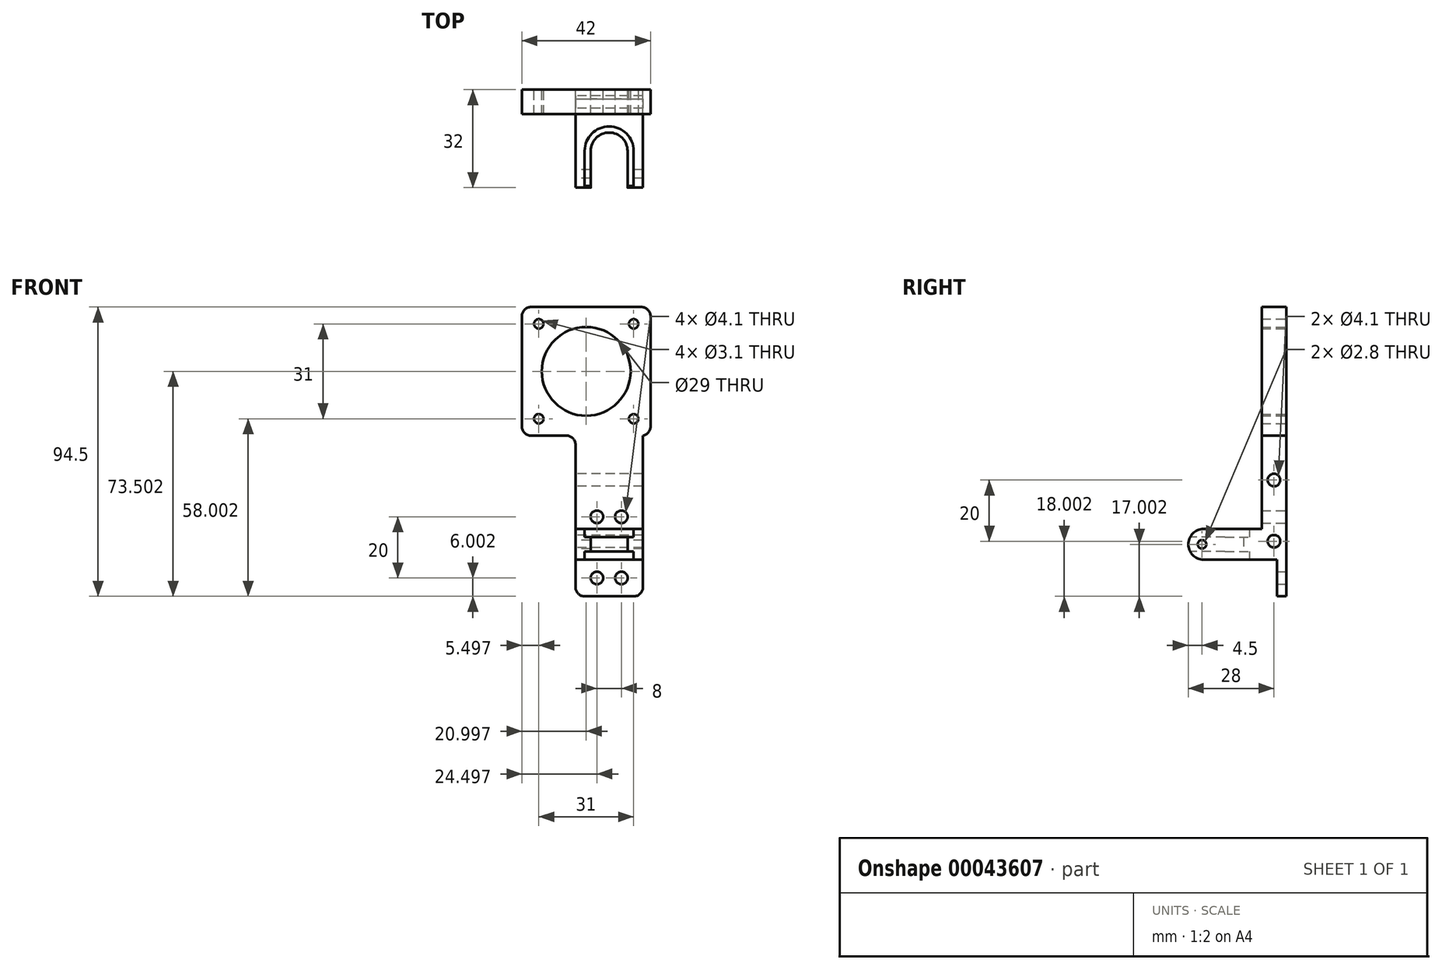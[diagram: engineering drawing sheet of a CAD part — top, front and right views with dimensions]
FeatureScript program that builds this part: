
annotation { "Feature Type Name" : "Feature", "Feature Type Description" : "" }
export const myFeature = defineFeature(function(context is Context, id is Id, definition is map)
    precondition{}
    {
        {
            var Q0;
            Q0=qCreatedBy(makeId("Front.planeOp"),FACE);
            var sketch = newSketch(context, id + "F0", { "sketchPlane" : qUnion([Q0])});
            skLineSegment(sketch, "E0.bottom", {"start": v(-39.92, 48.94) * mm, "end": v(-17.92, 48.94) * mm});
            skLineSegment(sketch, "E0.top", {"start": v(-39.92, 6.94) * mm, "end": v(-17.92, 6.94) * mm});
            skLineSegment(sketch, "E0.left", {"start": v(-39.92, 48.94) * mm, "end": v(-39.92, 6.94) * mm});
            skLineSegment(sketch, "E0.right", {"start": v(-17.92, 48.94) * mm, "end": v(-17.92, 6.94) * mm});
            skPoint(sketch, "E1", {"position": v(-32.92, 12.94) * mm});
            skPoint(sketch, "E2", {"position": v(-24.92, 12.94) * mm});
            skPoint(sketch, "E3", {"position": v(-24.92, 32.94) * mm});
            skPoint(sketch, "E4", {"position": v(-32.92, 32.94) * mm});
            skLineSegment(sketch, "E5", {"start": v(-39.92, 23.94) * mm, "end": v(-17.92, 23.94) * mm, "construction": true});
            skSolve(sketch);
        }
        {
            var Q0;
            Q0=makeQuery(id+"F0.imprint","IMPRINT",FACE,{"disambiguationData":[TD([[makeQuery(id+"F0.imprint","IMPRINT",EDGE,{"derivedFrom":sQuery(id+"F0.wireOp",EDGE,"E0.bottom")}),-1.0]])]});
            extrude(context, id + "F1", {"entities" : qUnion([Q0]), "depth" : 3 * mm});
        }
        {
            var Q0;
            Q0=makeQuery(id+"F1.opExtrude","SWEPT_FACE",FACE,{"disambiguationData":[OSD([sQuery(id+"F0.wireOp",EDGE,"E0.left")])]});
            var sketch = newSketch(context, id + "F2", { "sketchPlane" : qUnion([Q0])});
            skLineSegment(sketch, "E6.bottom", {"start": v(0, 18.94) * mm, "end": v(8, 18.94) * mm});
            skLineSegment(sketch, "E6.top", {"start": v(0, 48.94) * mm, "end": v(8, 48.94) * mm});
            skLineSegment(sketch, "E6.left", {"start": v(0, 18.94) * mm, "end": v(0, 48.94) * mm});
            skLineSegment(sketch, "E6.right", {"start": v(8, 18.94) * mm, "end": v(8, 48.94) * mm});
            skPoint(sketch, "E7", {"position": v(4, 44.94) * mm});
            skPoint(sketch, "E8", {"position": v(4, 24.94) * mm});
            skSolve(sketch);
        }
        {
            var Q0;
            {var subQ0=sQuery(id+"F2.wireOp",EDGE,"E6.left");Q0=makeQuery(id+"F2.imprint","IMPRINT",FACE,{"disambiguationData":[TD([[makeQuery(id+"F2.imprint","IMPRINT",EDGE,{"derivedFrom":subQ0}),1.0]])]});}
            var Q1;
            {var subQ0=sQuery(id+"F2.wireOp",EDGE,"E6.right");Q1=makeQuery(id+"F2.imprint","IMPRINT",FACE,{"disambiguationData":[TD([[makeQuery(id+"F2.imprint","IMPRINT",EDGE,{"derivedFrom":subQ0}),1.0]])]});}
            extrude(context, id + "F3", {"entities" : qUnion([Q0, Q1]), "operationType" : NewBodyOperationType.ADD, "oppositeDirection" : true, "depth" : 22 * mm});
        }
        {
            var Q0;
            Q0=sQuery(id+"F0.wireOp",VERTEX,"E2");
            var Q1;
            Q1=sQuery(id+"F0.wireOp",VERTEX,"E1");
            var Q2;
            Q2=sQuery(id+"F0.wireOp",VERTEX,"E4");
            var Q3;
            Q3=sQuery(id+"F0.wireOp",VERTEX,"E3");
            var Q4;
            Q4=makeQuery(id+"F1.opExtrude","SWEPT_BODY",BODY,{"disambiguationData":[OSD([sQuery(id+"F0.wireOp",EDGE,"E0.bottom"),sQuery(id+"F0.wireOp",EDGE,"E0.top"),sQuery(id+"F0.wireOp",EDGE,"E0.left"),sQuery(id+"F0.wireOp",EDGE,"E0.right")])]});
            hole(context, id + "F4", {"style" : HoleStyle.SIMPLE, "holeDiameter" : 4.1 * mm, "endStyle" : HoleEndStyle.THROUGH, "oppositeDirection" : true, "locations" : qUnion([Q0, Q1, Q2, Q3]), "scope" : qUnion([Q4])});
        }
        {
            var Q0;
            Q0=sQuery(id+"F0.wireOp",EDGE,"E5");
            cPlane(context, id + "F5", {"entities" : qUnion([Q0]), "cplaneType" : CPlaneType.LINE_ANGLE, "offset" : 150 * mm, "angle" : 90 * degree, "width" : 150 * mm, "height" : 150 * mm});
        }
        {
            var Q0;
            Q0=qCreatedBy(id+"F5.planeOp",FACE);
            var sketch = newSketch(context, id + "F6", { "sketchPlane" : qUnion([Q0])});
            skPoint(sketch, "E9", {"position": v(-28.92, -20) * mm});
            skCircle(sketch, "E10", {"center": v(-28.92, -20) * mm, "radius": 6 * mm});
            skCircle(sketch, "E11", {"center": v(-28.92, -20) * mm, "radius": 8 * mm});
            skLineSegment(sketch, "E12.top", {"start": v(-39.92, 0) * mm, "end": v(-17.92, 0) * mm});
            skLineSegment(sketch, "E13.bottom", {"start": v(-39.92, -32) * mm, "end": v(-17.92, -32) * mm});
            skLineSegment(sketch, "E13.left", {"start": v(-39.92, -32) * mm, "end": v(-39.92, 0) * mm});
            skLineSegment(sketch, "E13.right", {"start": v(-17.92, -32) * mm, "end": v(-17.92, 0) * mm});
            skLineSegment(sketch, "E14", {"start": v(-34.92, -20) * mm, "end": v(-34.92, -32) * mm});
            skLineSegment(sketch, "E15", {"start": v(-36.92, -20) * mm, "end": v(-36.92, -32) * mm});
            skLineSegment(sketch, "E16", {"start": v(-22.92, -20) * mm, "end": v(-22.92, -32) * mm});
            skLineSegment(sketch, "E17", {"start": v(-20.92, -20) * mm, "end": v(-20.92, -32) * mm});
            skPoint(sketch, "E18", {"position": v(-28.92, -27.5) * mm});
            skPoint(sketch, "E18.positionSnap0", {"position": v(-28.92, -32) * mm});
            skSolve(sketch);
        }
        {
            var Q0;
            Q0=makeQuery(id+"F6.imprint","IMPRINT",FACE,{"disambiguationData":[TD([[makeQuery(id+"F6.imprint","IMPRINT",EDGE,{"derivedFrom":sQuery(id+"F6.wireOp",EDGE,"E12.top")}),-1.0]])]});
            var Q1;
            Q1=sQuery(id+"F6.wireOp",EDGE,"E12.bottom");
            extrude(context, id + "F7", {"entities" : qUnion([Q0]), "operationType" : NewBodyOperationType.ADD, "surfaceEntities" : qUnion([Q1]), "endBound" : BoundingType.SYMMETRIC, "depth" : 10 * mm});
        }
        {
            var Q0;
            {var subQ5=sQuery(id+"F6.wireOp",EDGE,"E14");var subQ7=sQuery(id+"F6.wireOp",EDGE,"E10");var subQ9=makeQuery(id+"F6.imprint","INTERSECT",VERTEX,{"derivedFrom":[subQ7,subQ5]});Q0=makeQuery(id+"F6.imprint","IMPRINT",FACE,{"disambiguationData":[TD([[makeQuery(id+"F6.imprint","IMPRINT",EDGE,{"disambiguationData":[TD([[subQ9,1.0]])],"derivedFrom":subQ7}),-1.0]])]});}
            var Q1;
            {var subQ0=sQuery(id+"F6.wireOp",EDGE,"E15");Q1=makeQuery(id+"F6.imprint","IMPRINT",FACE,{"disambiguationData":[TD([[makeQuery(id+"F6.imprint","IMPRINT",EDGE,{"derivedFrom":subQ0}),1.0]])]});}
            var Q2;
            {var subQ0=sQuery(id+"F6.wireOp",EDGE,"E17");Q2=makeQuery(id+"F6.imprint","IMPRINT",FACE,{"disambiguationData":[TD([[makeQuery(id+"F6.imprint","IMPRINT",EDGE,{"derivedFrom":subQ0}),-1.0]])]});}
            extrude(context, id + "F8", {"entities" : qUnion([Q0, Q1, Q2]), "operationType" : NewBodyOperationType.ADD, "endBound" : BoundingType.SYMMETRIC, "depth" : 4.65 * mm});
        }
        {
            var Q0;
            {var subQ0=sQuery(id+"F6.wireOp",EDGE,"E13.bottom");Q0=makeQuery(id+"F7.opExtrude","CAP_EDGE",EDGE,{"disambiguationData":[OSD([subQ0]),TDD([makeQuery(id+"F6.imprint","IMPRINT",EDGE,{"disambiguationData":[TD([[makeQuery(id+"F6.imprint","INTERSECT",VERTEX,{"derivedFrom":[subQ0,sQuery(id+"F6.wireOp",EDGE,"E13.left")]}),-1.0]])],"derivedFrom":subQ0})])],"isStart":false});}
            var Q1;
            {var subQ0=sQuery(id+"F6.wireOp",EDGE,"E13.bottom");Q1=makeQuery(id+"F7.opExtrude","CAP_EDGE",EDGE,{"disambiguationData":[OSD([subQ0]),TDD([makeQuery(id+"F6.imprint","IMPRINT",EDGE,{"disambiguationData":[TD([[makeQuery(id+"F6.imprint","INTERSECT",VERTEX,{"derivedFrom":[subQ0,sQuery(id+"F6.wireOp",EDGE,"E13.left")]}),-1.0]])],"derivedFrom":subQ0})])],"isStart":true});}
            var Q2;
            {var subQ0=sQuery(id+"F6.wireOp",EDGE,"E13.bottom");Q2=makeQuery(id+"F7.opExtrude","CAP_EDGE",EDGE,{"disambiguationData":[OSD([subQ0]),TDD([makeQuery(id+"F6.imprint","IMPRINT",EDGE,{"disambiguationData":[TD([[makeQuery(id+"F6.imprint","INTERSECT",VERTEX,{"derivedFrom":[subQ0,sQuery(id+"F6.wireOp",EDGE,"E13.right")]}),1.0]])],"derivedFrom":subQ0})])],"isStart":true});}
            var Q3;
            {var subQ0=sQuery(id+"F6.wireOp",EDGE,"E13.bottom");Q3=makeQuery(id+"F7.opExtrude","CAP_EDGE",EDGE,{"disambiguationData":[OSD([subQ0]),TDD([makeQuery(id+"F6.imprint","IMPRINT",EDGE,{"disambiguationData":[TD([[makeQuery(id+"F6.imprint","INTERSECT",VERTEX,{"derivedFrom":[subQ0,sQuery(id+"F6.wireOp",EDGE,"E13.right")]}),1.0]])],"derivedFrom":subQ0})])],"isStart":false});}
            fillet(context, id + "F9", {"entities" : qUnion([Q0, Q1, Q2, Q3]), "radius" : 5 * mm, "tangentPropagation" : true, "allowEdgeOverflow" : false});
        }
        {
            var Q0;
            Q0=makeQuery(id+"F7.boolean.opBoolean","MERGE",FACE,{"derivedFrom":[makeQuery(id+"F3.boolean.opBoolean","MERGE",FACE,{"derivedFrom":[makeQuery(id+"F1.opExtrude","SWEPT_FACE",FACE,{"disambiguationData":[OSD([sQuery(id+"F0.wireOp",EDGE,"E0.left")])]}),makeQuery(id+"F3.opExtrude","CAP_FACE",FACE,{"disambiguationData":[OSD([sQuery(id+"F2.wireOp",EDGE,"E6.bottom"),sQuery(id+"F2.wireOp",EDGE,"E6.top"),sQuery(id+"F2.wireOp",EDGE,"E6.left"),sQuery(id+"F2.wireOp",EDGE,"E6.right")])],"isStart":true})]}),makeQuery(id+"F7.opExtrude","SWEPT_FACE",FACE,{"disambiguationData":[OSD([sQuery(id+"F6.wireOp",EDGE,"E13.left")])]})]});
            var sketch = newSketch(context, id + "F10", { "sketchPlane" : qUnion([Q0])});
            skPoint(sketch, "E19", {"position": v(27.5, 23.94) * mm});
            skSolve(sketch);
        }
        {
            var Q0;
            Q0=sQuery(id+"F2.wireOp",VERTEX,"E7");
            var Q1;
            Q1=sQuery(id+"F2.wireOp",VERTEX,"E8");
            var Q2;
            Q2=makeQuery(id+"F1.opExtrude","SWEPT_BODY",BODY,{"disambiguationData":[OSD([sQuery(id+"F0.wireOp",EDGE,"E0.bottom"),sQuery(id+"F0.wireOp",EDGE,"E0.top"),sQuery(id+"F0.wireOp",EDGE,"E0.left"),sQuery(id+"F0.wireOp",EDGE,"E0.right")])]});
            hole(context, id + "F11", {"style" : HoleStyle.SIMPLE, "holeDiameter" : 4.1 * mm, "endStyle" : HoleEndStyle.THROUGH, "locations" : qUnion([Q0, Q1]), "scope" : qUnion([Q2])});
        }
        {
            var Q0;
            Q0=sQuery(id+"F10.wireOp",VERTEX,"E19");
            var Q1;
            Q1=makeQuery(id+"F1.opExtrude","SWEPT_BODY",BODY,{"disambiguationData":[OSD([sQuery(id+"F0.wireOp",EDGE,"E0.bottom"),sQuery(id+"F0.wireOp",EDGE,"E0.top"),sQuery(id+"F0.wireOp",EDGE,"E0.left"),sQuery(id+"F0.wireOp",EDGE,"E0.right")])]});
            hole(context, id + "F12", {"style" : HoleStyle.SIMPLE, "holeDiameter" : 2.8 * mm, "endStyle" : HoleEndStyle.THROUGH, "locations" : qUnion([Q0]), "scope" : qUnion([Q1])});
        }
        {
            var Q0;
            Q0=qCreatedBy(makeId("Front.planeOp"),FACE);
            var sketch = newSketch(context, id + "F13", { "sketchPlane" : qUnion([Q0])});
            skLineSegment(sketch, "E20.bottom", {"start": v(-39.92, 48.94) * mm, "end": v(-17.92, 48.94) * mm});
            skLineSegment(sketch, "E20.top", {"start": v(-39.92, 59.44) * mm, "end": v(-17.92, 59.44) * mm});
            skLineSegment(sketch, "E20.left", {"start": v(-39.92, 48.94) * mm, "end": v(-39.92, 59.44) * mm});
            skLineSegment(sketch, "E20.right", {"start": v(-17.92, 48.94) * mm, "end": v(-17.92, 59.44) * mm});
            skPoint(sketch, "E21.firstSnap0", {"position": v(-28.92, 59.44) * mm});
            skLineSegment(sketch, "E21.bottom", {"start": v(-15.42, 59.44) * mm, "end": v(-57.42, 59.44) * mm});
            skLineSegment(sketch, "E21.top", {"start": v(-15.42, 101.44) * mm, "end": v(-57.42, 101.44) * mm});
            skLineSegment(sketch, "E21.left", {"start": v(-15.42, 59.44) * mm, "end": v(-15.42, 101.44) * mm});
            skLineSegment(sketch, "E21.right", {"start": v(-57.42, 59.44) * mm, "end": v(-57.42, 101.44) * mm});
            skPoint(sketch, "E22", {"position": v(-36.42, 80.44) * mm});
            skPoint(sketch, "E23", {"position": v(-51.92, 95.94) * mm});
            skPoint(sketch, "E24", {"position": v(-51.92, 64.94) * mm});
            skPoint(sketch, "E25", {"position": v(-20.92, 64.94) * mm});
            skPoint(sketch, "E26", {"position": v(-20.92, 95.94) * mm});
            skLineSegment(sketch, "E27", {"start": v(-28.92, 101.44) * mm, "end": v(-28.92, 59.44) * mm, "construction": true});
            skLineSegment(sketch, "E28", {"start": v(-28.92, 7.33) * mm, "end": v(-28.92, 59.44) * mm, "construction": true});
            skSolve(sketch);
        }
        {
            var Q0;
            Q0=makeQuery(id+"F13.imprint","IMPRINT",FACE,{"disambiguationData":[TD([[makeQuery(id+"F13.imprint","IMPRINT",EDGE,{"derivedFrom":sQuery(id+"F13.wireOp",EDGE,"E21.top")}),1.0]])]});
            var Q1;
            Q1=makeQuery(id+"F13.imprint","IMPRINT",FACE,{"disambiguationData":[TD([[makeQuery(id+"F13.imprint","IMPRINT",EDGE,{"derivedFrom":sQuery(id+"F13.wireOp",EDGE,"E20.bottom")}),1.0]])]});
            extrude(context, id + "F14", {"entities" : qUnion([Q0, Q1]), "operationType" : NewBodyOperationType.ADD, "depth" : 8 * mm});
        }
        {
            var Q0;
            Q0=makeQuery(id+"F14.opExtrude","SWEPT_EDGE",EDGE,{"disambiguationData":[OSD([sQuery(id+"F13.wireOp",EDGE,"E21.top"),sQuery(id+"F13.wireOp",EDGE,"E21.right")])]});
            var Q1;
            Q1=makeQuery(id+"F14.opExtrude","SWEPT_EDGE",EDGE,{"disambiguationData":[OSD([sQuery(id+"F13.wireOp",EDGE,"E21.bottom"),sQuery(id+"F13.wireOp",EDGE,"E21.right")])]});
            var Q2;
            Q2=makeQuery(id+"F14.opExtrude","SWEPT_EDGE",EDGE,{"disambiguationData":[OSD([sQuery(id+"F13.wireOp",EDGE,"E21.top"),sQuery(id+"F13.wireOp",EDGE,"E21.left")])]});
            var Q3;
            Q3=makeQuery(id+"F1.opExtrude","SWEPT_EDGE",EDGE,{"disambiguationData":[OSD([sQuery(id+"F0.wireOp",EDGE,"E0.top"),sQuery(id+"F0.wireOp",EDGE,"E0.left")])]});
            var Q4;
            Q4=makeQuery(id+"F1.opExtrude","SWEPT_EDGE",EDGE,{"disambiguationData":[OSD([sQuery(id+"F0.wireOp",EDGE,"E0.top"),sQuery(id+"F0.wireOp",EDGE,"E0.right")])]});
            var Q5;
            Q5=makeQuery(id+"F14.opExtrude","SWEPT_EDGE",EDGE,{"disambiguationData":[OSD([sQuery(id+"F13.wireOp",EDGE,"E20.left"),sQuery(id+"F13.wireOp",EDGE,"E21.bottom")])]});
            var Q6;
            Q6=makeQuery(id+"F14.opExtrude","SWEPT_EDGE",EDGE,{"disambiguationData":[OSD([sQuery(id+"F13.wireOp",EDGE,"E21.bottom"),sQuery(id+"F13.wireOp",EDGE,"E21.left")])]});
            fillet(context, id + "F15", {"entities" : qUnion([Q0, Q1, Q2, Q3, Q4, Q5, Q6]), "radius" : 3 * mm, "tangentPropagation" : true, "allowEdgeOverflow" : false});
        }
        {
            var Q0;
            Q0=sQuery(id+"F13.wireOp",VERTEX,"E22");
            var Q1;
            Q1=makeQuery(id+"F1.opExtrude","SWEPT_BODY",BODY,{"disambiguationData":[OSD([sQuery(id+"F0.wireOp",EDGE,"E0.bottom"),sQuery(id+"F0.wireOp",EDGE,"E0.top"),sQuery(id+"F0.wireOp",EDGE,"E0.left"),sQuery(id+"F0.wireOp",EDGE,"E0.right")])]});
            hole(context, id + "F16", {"style" : HoleStyle.SIMPLE, "holeDiameter" : 29 * mm, "endStyle" : HoleEndStyle.THROUGH, "oppositeDirection" : true, "locations" : qUnion([Q0]), "scope" : qUnion([Q1])});
        }
        {
            var Q0;
            Q0=sQuery(id+"F13.wireOp",VERTEX,"E23");
            var Q1;
            Q1=sQuery(id+"F13.wireOp",VERTEX,"E26");
            var Q2;
            Q2=sQuery(id+"F13.wireOp",VERTEX,"E25");
            var Q3;
            Q3=sQuery(id+"F13.wireOp",VERTEX,"E24");
            var Q4;
            Q4=makeQuery(id+"F1.opExtrude","SWEPT_BODY",BODY,{"disambiguationData":[OSD([sQuery(id+"F0.wireOp",EDGE,"E0.bottom"),sQuery(id+"F0.wireOp",EDGE,"E0.top"),sQuery(id+"F0.wireOp",EDGE,"E0.left"),sQuery(id+"F0.wireOp",EDGE,"E0.right")])]});
            hole(context, id + "F17", {"style" : HoleStyle.SIMPLE, "holeDiameter" : 3.1 * mm, "endStyle" : HoleEndStyle.THROUGH, "oppositeDirection" : true, "locations" : qUnion([Q0, Q1, Q2, Q3]), "scope" : qUnion([Q4])});
        }
    });
